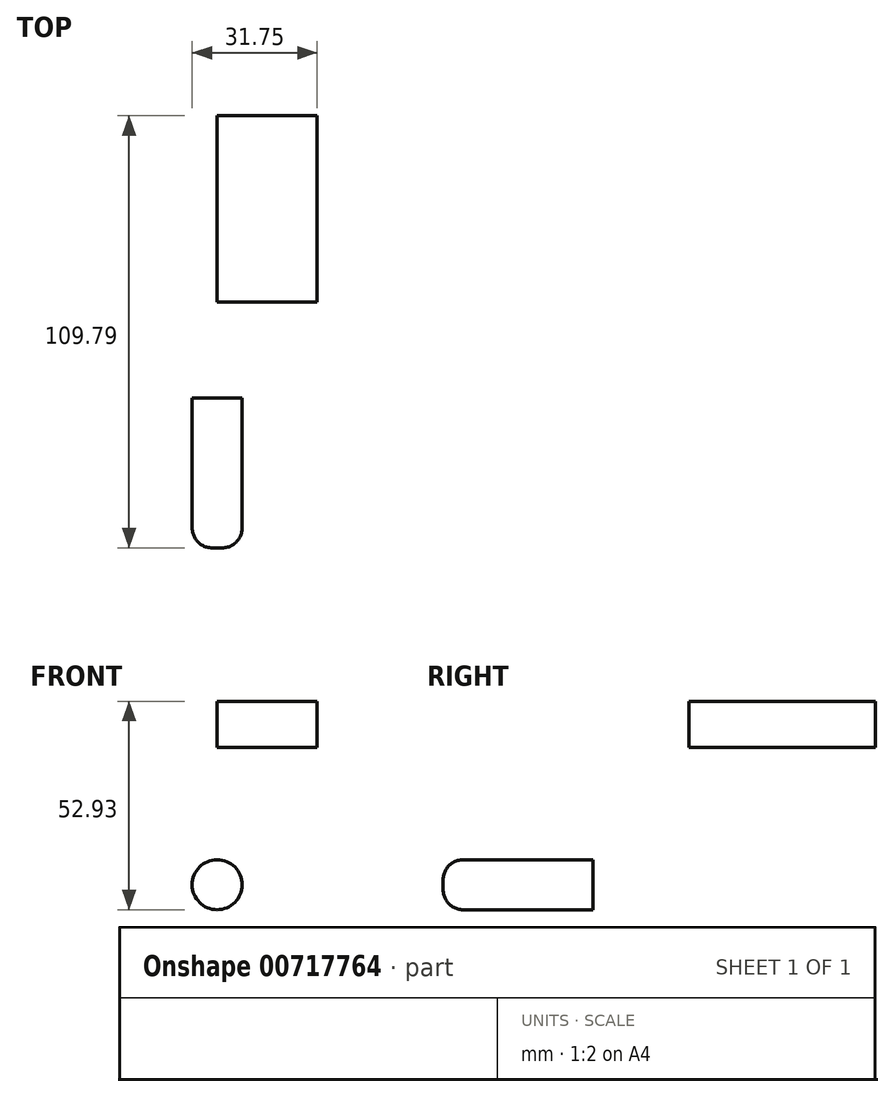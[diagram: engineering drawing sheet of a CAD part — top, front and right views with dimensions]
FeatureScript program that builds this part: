
annotation { "Feature Type Name" : "Feature", "Feature Type Description" : "" }
export const myFeature = defineFeature(function(context is Context, id is Id, definition is map)
    precondition{}
    {
        {
            var Q0;
            Q0=qCreatedBy(makeId("Front.planeOp"),FACE);
            var sketch = newSketch(context, id + "F0", { "sketchPlane" : qUnion([Q0])});
            skCircle(sketch, "E0", {"center": v(0, 0) * mm, "radius": 6.35 * mm});
            skSolve(sketch);
        }
        {
            var Q0;
            Q0 = qSketchRegion(id + "F0", true);
            extrude(context, id + "F1", {"entities" : qUnion([Q0]), "depth" : 38.1 * mm, "offsetDistance" : 25.4 * mm});
        }
        {
            var Q0;
            Q0=makeQuery(id+"F1.opExtrude","CAP_EDGE",EDGE,{"disambiguationData":[OSD([sQuery(id+"F0.wireOp",EDGE,"E0")])],"isStart":false});
            fillet(context, id + "F2", {"entities" : qUnion([Q0]), "radius" : 5.08 * mm, "tangentPropagation" : true, "allowEdgeOverflow" : false});
        }
        {
            var Q0;
            Q0=qCreatedBy(makeId("Right.planeOp"),FACE);
            var sketch = newSketch(context, id + "F3", { "sketchPlane" : qUnion([Q0])});
            skLineSegment(sketch, "E1.bottom", {"start": v(71.69, 46.58) * mm, "end": v(24.38, 46.58) * mm});
            skLineSegment(sketch, "E1.top", {"start": v(71.69, 34.9) * mm, "end": v(24.38, 34.9) * mm});
            skLineSegment(sketch, "E1.left", {"start": v(71.69, 46.58) * mm, "end": v(71.69, 34.9) * mm});
            skLineSegment(sketch, "E1.right", {"start": v(24.38, 46.58) * mm, "end": v(24.38, 34.9) * mm});
            skSolve(sketch);
        }
        {
            var Q0;
            Q0 = qSketchRegion(id + "F3", true);
            extrude(context, id + "F4", {"entities" : qUnion([Q0]), "depth" : 25.4 * mm, "offsetDistance" : 25.4 * mm});
        }
    });
